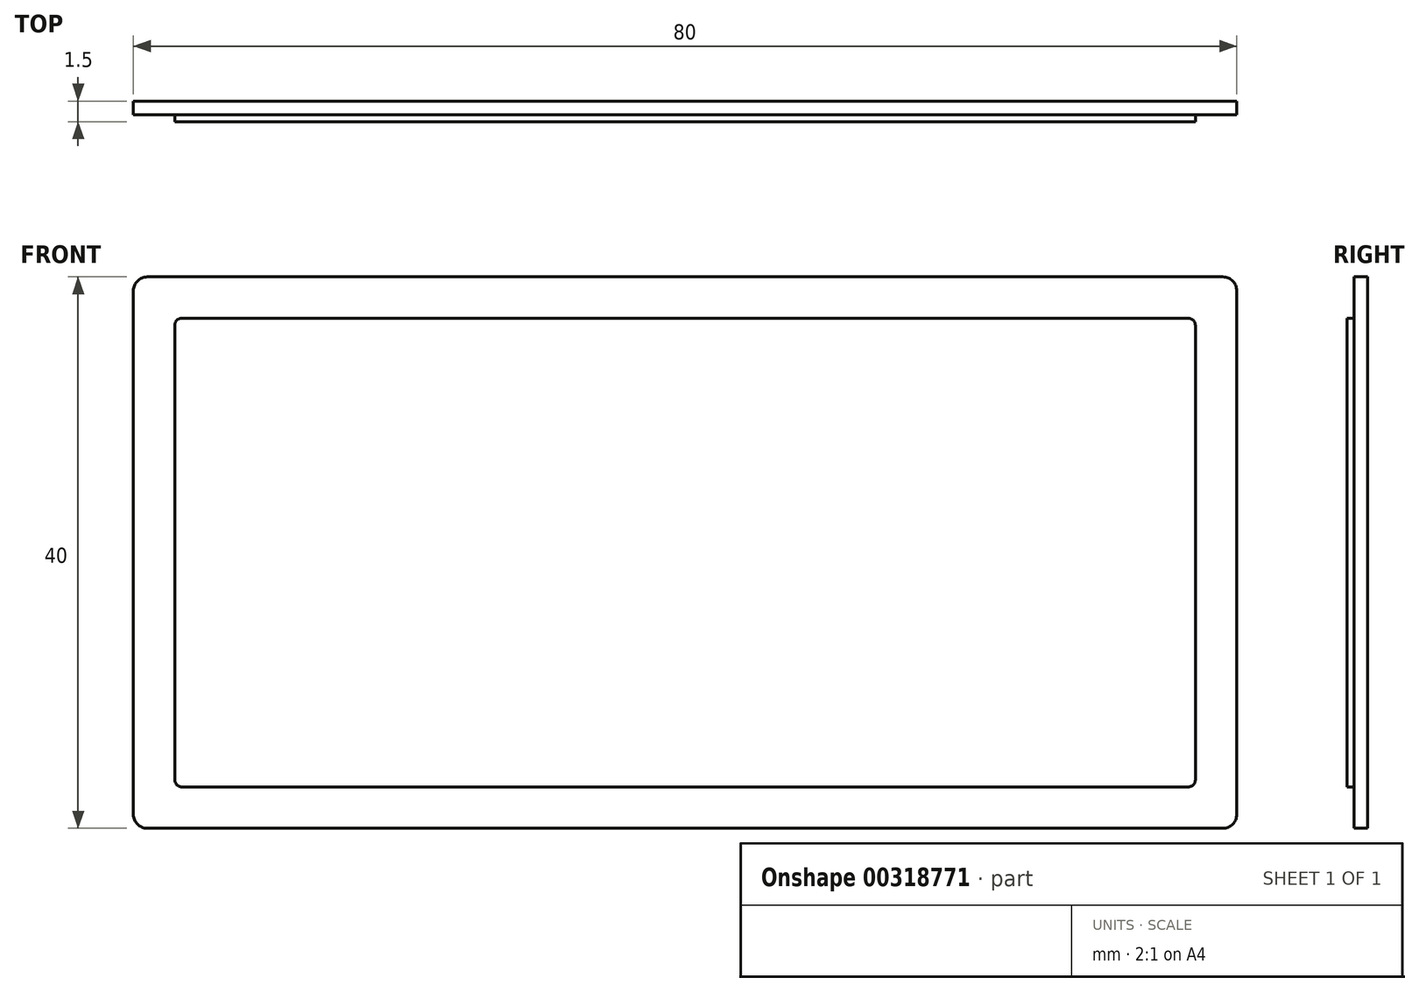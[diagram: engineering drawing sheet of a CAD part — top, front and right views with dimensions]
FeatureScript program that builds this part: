
annotation { "Feature Type Name" : "Feature", "Feature Type Description" : "" }
export const myFeature = defineFeature(function(context is Context, id is Id, definition is map)
    precondition{}
    {
        {
            var Q0;
            Q0=qCreatedBy(makeId("Front.planeOp"),FACE);
            var sketch = newSketch(context, id + "F0", { "sketchPlane" : qUnion([Q0])});
            skLineSegment(sketch, "E0.bottom", {"start": v(40, 20) * mm, "end": v(-40, 20) * mm});
            skLineSegment(sketch, "E0.top", {"start": v(40, -20) * mm, "end": v(-40, -20) * mm});
            skLineSegment(sketch, "E0.left", {"start": v(40, 20) * mm, "end": v(40, -20) * mm});
            skLineSegment(sketch, "E0.right", {"start": v(-40, 20) * mm, "end": v(-40, -20) * mm});
            skPoint(sketch, "E0.middle", {"position": v(0, 0) * mm});
            skSolve(sketch);
        }
        {
            var Q0;
            Q0=makeQuery(id+"F0.imprint","IMPRINT",FACE,{"disambiguationData":[TD([[makeQuery(id+"F0.imprint","IMPRINT",EDGE,{"derivedFrom":sQuery(id+"F0.wireOp",EDGE,"E0.bottom")}),1.0]])]});
            extrude(context, id + "F1", {"entities" : qUnion([Q0]), "depth" : 1 * mm, "offsetDistance" : 25 * mm});
        }
        {
            var Q0;
            Q0=makeQuery(id+"F1.opExtrude","CAP_FACE",FACE,{"disambiguationData":[OSD([sQuery(id+"F0.wireOp",EDGE,"E0.bottom"),sQuery(id+"F0.wireOp",EDGE,"E0.top"),sQuery(id+"F0.wireOp",EDGE,"E0.left"),sQuery(id+"F0.wireOp",EDGE,"E0.right")])],"isStart":false});
            var sketch = newSketch(context, id + "F2", { "sketchPlane" : qUnion([Q0])});
            skLineSegment(sketch, "E1.bottom", {"start": v(37, 17) * mm, "end": v(-37, 17) * mm});
            skLineSegment(sketch, "E1.top", {"start": v(37, -17) * mm, "end": v(-37, -17) * mm});
            skLineSegment(sketch, "E1.left", {"start": v(37, 17) * mm, "end": v(37, -17) * mm});
            skLineSegment(sketch, "E1.right", {"start": v(-37, 17) * mm, "end": v(-37, -17) * mm});
            skPoint(sketch, "E1.middle", {"position": v(0, 0) * mm});
            skSolve(sketch);
        }
        {
            var Q0;
            Q0=makeQuery(id+"F2.imprint","IMPRINT",FACE,{"disambiguationData":[TD([[makeQuery(id+"F2.imprint","IMPRINT",EDGE,{"derivedFrom":sQuery(id+"F2.wireOp",EDGE,"E1.bottom")}),1.0]])]});
            extrude(context, id + "F3", {"entities" : qUnion([Q0]), "operationType" : NewBodyOperationType.ADD, "depth" : 0.5 * mm, "offsetDistance" : 25 * mm});
        }
        {
            var Q0;
            Q0=makeQuery(id+"F1.opExtrude","SWEPT_EDGE",EDGE,{"disambiguationData":[OSD([sQuery(id+"F0.wireOp",EDGE,"E0.bottom"),sQuery(id+"F0.wireOp",EDGE,"E0.left")])]});
            var Q1;
            Q1=makeQuery(id+"F1.opExtrude","SWEPT_EDGE",EDGE,{"disambiguationData":[OSD([sQuery(id+"F0.wireOp",EDGE,"E0.top"),sQuery(id+"F0.wireOp",EDGE,"E0.left")])]});
            var Q2;
            Q2=makeQuery(id+"F1.opExtrude","SWEPT_EDGE",EDGE,{"disambiguationData":[OSD([sQuery(id+"F0.wireOp",EDGE,"E0.top"),sQuery(id+"F0.wireOp",EDGE,"E0.right")])]});
            var Q3;
            Q3=makeQuery(id+"F1.opExtrude","SWEPT_EDGE",EDGE,{"disambiguationData":[OSD([sQuery(id+"F0.wireOp",EDGE,"E0.bottom"),sQuery(id+"F0.wireOp",EDGE,"E0.right")])]});
            fillet(context, id + "F4", {"entities" : qUnion([Q0, Q1, Q2, Q3]), "radius" : 1 * mm, "tangentPropagation" : true, "allowEdgeOverflow" : false});
        }
        {
            var Q0;
            Q0=makeQuery(id+"F3.opExtrude","SWEPT_EDGE",EDGE,{"disambiguationData":[OSD([sQuery(id+"F2.wireOp",EDGE,"E1.bottom"),sQuery(id+"F2.wireOp",EDGE,"E1.right")])]});
            var Q1;
            Q1=makeQuery(id+"F3.opExtrude","SWEPT_EDGE",EDGE,{"disambiguationData":[OSD([sQuery(id+"F2.wireOp",EDGE,"E1.top"),sQuery(id+"F2.wireOp",EDGE,"E1.right")])]});
            var Q2;
            Q2=makeQuery(id+"F3.opExtrude","SWEPT_EDGE",EDGE,{"disambiguationData":[OSD([sQuery(id+"F2.wireOp",EDGE,"E1.top"),sQuery(id+"F2.wireOp",EDGE,"E1.left")])]});
            var Q3;
            Q3=makeQuery(id+"F3.opExtrude","SWEPT_EDGE",EDGE,{"disambiguationData":[OSD([sQuery(id+"F2.wireOp",EDGE,"E1.bottom"),sQuery(id+"F2.wireOp",EDGE,"E1.left")])]});
            fillet(context, id + "F5", {"entities" : qUnion([Q0, Q1, Q2, Q3]), "radius" : 0.5 * mm, "tangentPropagation" : true, "allowEdgeOverflow" : false});
        }
    });
